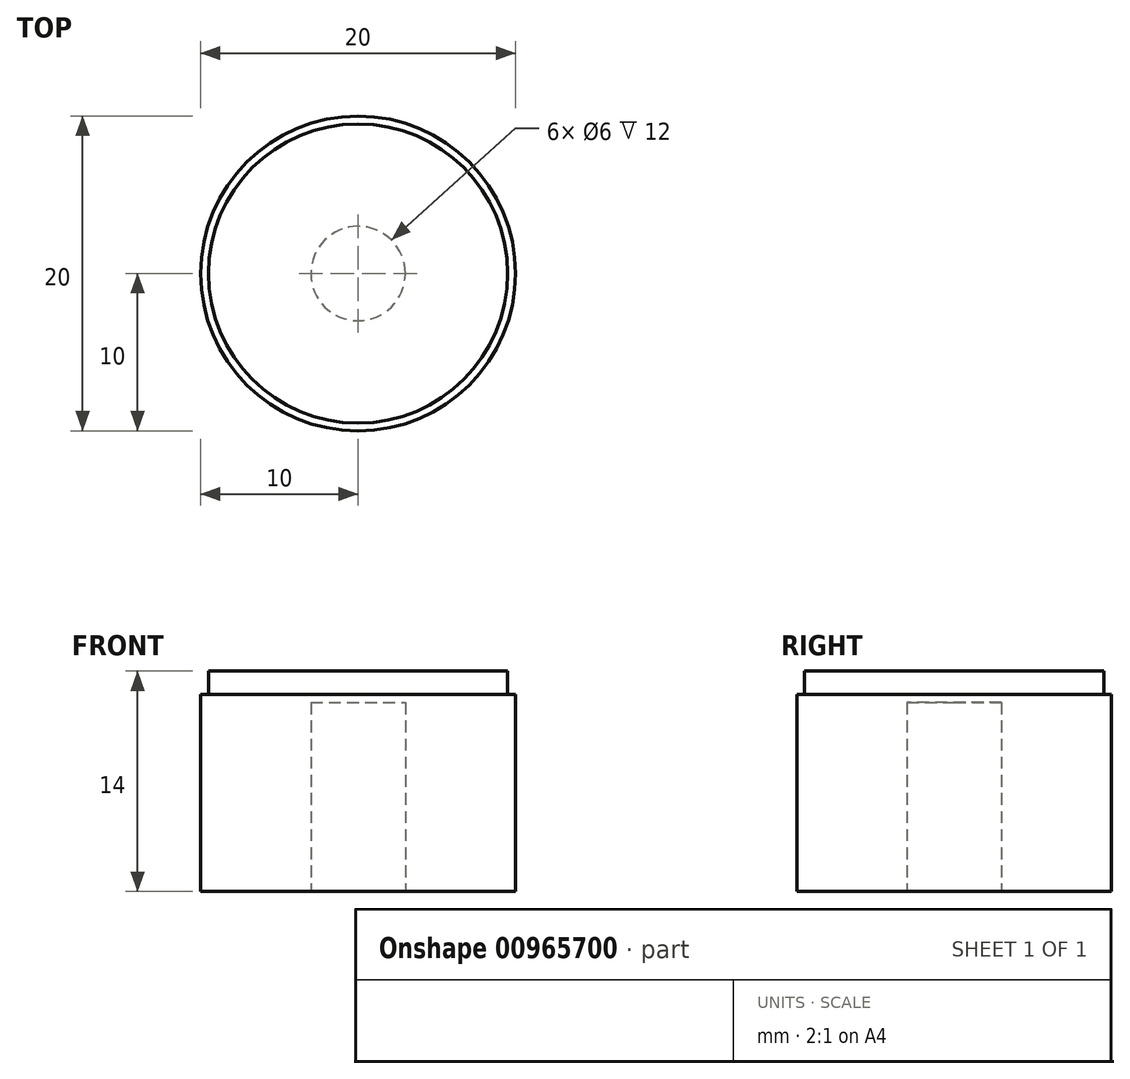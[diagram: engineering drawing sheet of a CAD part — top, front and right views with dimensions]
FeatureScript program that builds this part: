
annotation { "Feature Type Name" : "Feature", "Feature Type Description" : "" }
export const myFeature = defineFeature(function(context is Context, id is Id, definition is map)
    precondition{}
    {
        {
            var Q0;
            Q0=qCreatedBy(makeId("Top.planeOp"),FACE);
            var sketch = newSketch(context, id + "F0", { "sketchPlane" : qUnion([Q0])});
            skCircle(sketch, "E0", {"center": v(0, 0) * mm, "radius": 10 * mm});
            skSolve(sketch);
        }
        {
            var Q0;
            Q0=qSketchRegion(id+"F0",true);
            extrude(context, id + "F1", {"entities" : qUnion([Q0]), "depth" : 14 * mm, "offsetDistance" : 25 * mm});
        }
        {
            var Q0;
            Q0=makeQuery(id+"F1.opExtrude","CAP_FACE",FACE,{"disambiguationData":[OSD([sQuery(id+"F0.wireOp",EDGE,"E0")])],"isStart":true});
            var sketch = newSketch(context, id + "F2", { "sketchPlane" : qUnion([Q0])});
            skCircle(sketch, "E1", {"center": v(0, 0) * mm, "radius": 3 * mm});
            skSolve(sketch);
        }
        {
            var Q0;
            Q0=qSketchRegion(id+"F2",true);
            extrude(context, id + "F3", {"entities" : qUnion([Q0]), "operationType" : NewBodyOperationType.REMOVE, "oppositeDirection" : true, "depth" : 12 * mm, "offsetDistance" : 25 * mm});
        }
        {
            var Q0;
            Q0=makeQuery(id+"F1.opExtrude","CAP_FACE",FACE,{"disambiguationData":[OSD([sQuery(id+"F0.wireOp",EDGE,"E0")])],"isStart":false});
            var sketch = newSketch(context, id + "F4", { "sketchPlane" : qUnion([Q0])});
            skCircle(sketch, "E2", {"center": v(0, 0) * mm, "radius": 9.5 * mm});
            skCircle(sketch, "E3", {"center": v(0, 0) * mm, "radius": 10 * mm});
            skSolve(sketch);
        }
        {
            var Q0;
            Q0=qSketchRegion(id+"F4",true);
            extrude(context, id + "F5", {"entities" : qUnion([Q0]), "operationType" : NewBodyOperationType.REMOVE, "oppositeDirection" : true, "depth" : 1.5 * mm, "offsetDistance" : 25 * mm});
        }
    });
